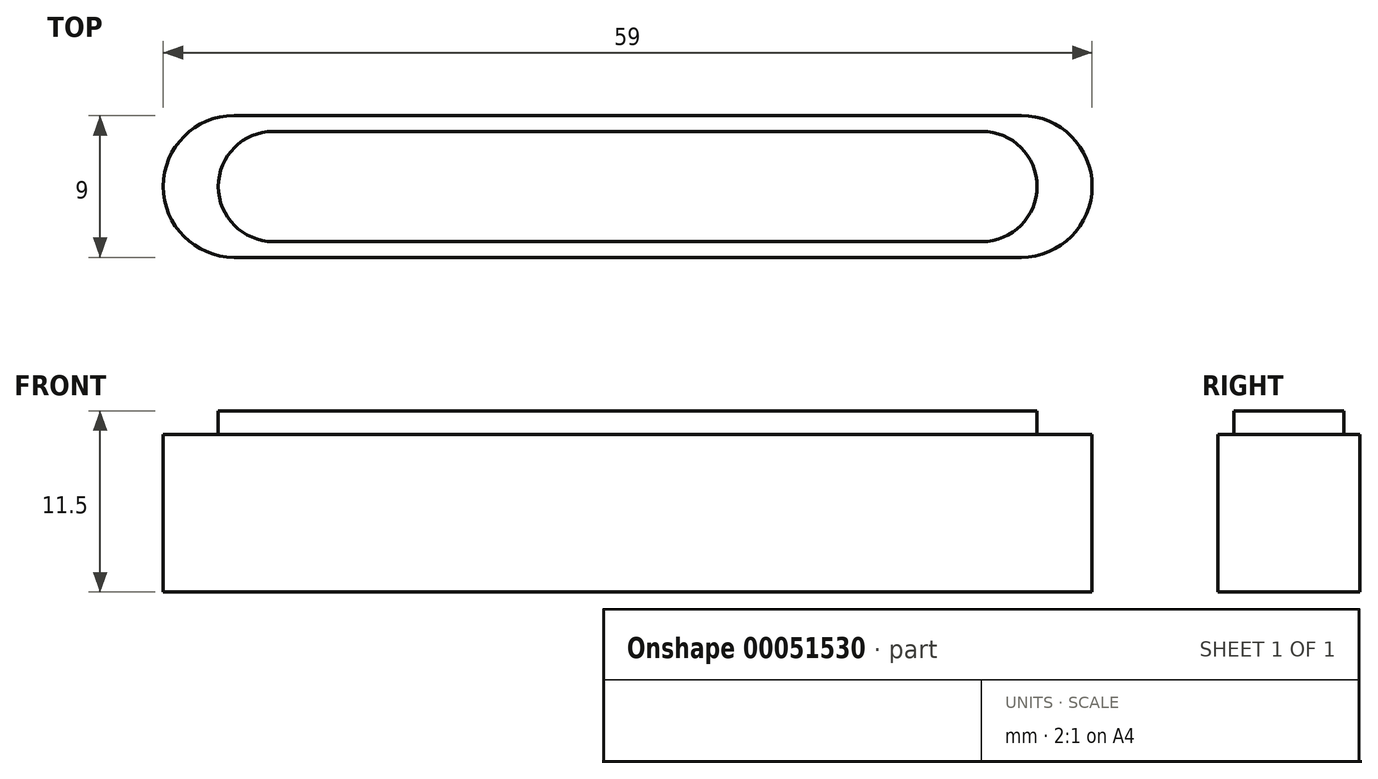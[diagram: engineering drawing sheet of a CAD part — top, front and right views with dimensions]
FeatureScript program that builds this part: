
annotation { "Feature Type Name" : "Feature", "Feature Type Description" : "" }
export const myFeature = defineFeature(function(context is Context, id is Id, definition is map)
    precondition{}
    {
        {
            assignVariable(context, id + "F0", {"name" : "pot_d", "anyValue" : 10 * mm});
        }
        {
            var Q0;
            Q0=qCreatedBy(makeId("Top.planeOp"),FACE);
            var sketch = newSketch(context, id + "F1", { "sketchPlane" : qUnion([Q0])});
            skLineSegment(sketch, "E0", {"start": v(-25, 0) * mm, "end": v(25, 0) * mm});
            skArc(sketch, "E1.0.startCap", {"start": v(-25, -4.5) * mm, "mid": v(-29.5, 0) * mm, "end": v(-25, 4.5) * mm});
            skArc(sketch, "E1.0.endCap", {"start": v(25, 4.5) * mm, "mid": v(29.5, 0) * mm, "end": v(25, -4.5) * mm});
            skLineSegment(sketch, "E1.0.left", {"start": v(-25, 4.5) * mm, "end": v(25, 4.5) * mm});
            skLineSegment(sketch, "E1.0.right", {"start": v(-25, -4.5) * mm, "end": v(25, -4.5) * mm});
            skSolve(sketch);
        }
        {
            var Q0;
            Q0 = qSketchRegion(id + "F1", true);
            extrude(context, id + "F2", {"entities" : qUnion([Q0]), "depth" : getVariable(context, 'pot_d')});
        }
        {
            assignVariable(context, id + "F3", {"name" : "lip_d", "anyValue" : 1.5 * mm});
        }
        {
            var Q0;
            Q0=makeQuery(id+"F2.opExtrude","CAP_FACE",FACE,{"disambiguationData":[OSD([sQuery(id+"F1.wireOp",EDGE,"E1.0.startCap"),sQuery(id+"F1.wireOp",EDGE,"E1.0.endCap"),sQuery(id+"F1.wireOp",EDGE,"E1.0.left"),sQuery(id+"F1.wireOp",EDGE,"E1.0.right")])],"isStart":false});
            var sketch = newSketch(context, id + "F4", { "sketchPlane" : qUnion([Q0])});
            skLineSegment(sketch, "E2", {"start": v(-22.5, 0) * mm, "end": v(22.5, 0) * mm});
            skArc(sketch, "E3.0.startCap", {"start": v(-22.5, -3.5) * mm, "mid": v(-26, 0) * mm, "end": v(-22.5, 3.5) * mm});
            skArc(sketch, "E3.0.endCap", {"start": v(22.5, 3.5) * mm, "mid": v(26, 0) * mm, "end": v(22.5, -3.5) * mm});
            skLineSegment(sketch, "E3.0.left", {"start": v(-22.5, 3.5) * mm, "end": v(22.5, 3.5) * mm});
            skLineSegment(sketch, "E3.0.right", {"start": v(-22.5, -3.5) * mm, "end": v(22.5, -3.5) * mm});
            skSolve(sketch);
        }
        {
            var Q0;
            Q0 = qSketchRegion(id + "F4", true);
            extrude(context, id + "F5", {"entities" : qUnion([Q0]), "operationType" : NewBodyOperationType.ADD, "depth" : getVariable(context, 'lip_d')});
        }
    });
